# Revit family: result
name_source: partatom
category: Specialty Equipment
revit_build: Autodesk Revit 2015 (Build: 20140903_1530(x64)
units: mm (PartAtom-declared; Revit-internal decimal feet)

## types (1)
- Default
    BIMobject category = Shower trays
    BIMobject category code = sanitary-shower-trays
    BIMobject main category = Sanitary
    BIMobject main category code = sanitary
    Brand url = http://www.duravit.com
    Edition number = 1
    GTIN code = https://4053424675206
    Installation instructions = https://pro.duravit.com
    Manufacturer name = DURAVIT
    Product Guid = ccfd1b15-9e73-4d90-a85e-1945c6291bb6
    Product SKU = tempano-square-shower-tray-720188
    Product data url = https://bimobject.com
    Product family = Tempano
    Product group = shower trays
    Product name = 720188-Tempano square shower tray
    Product url = https://pro.duravit.com
    QR code = http://bimobject.com
    Technical description = https://pro.duravit.com
    Youtube clip = https://pro.duravit.com

## geometry (parser evidence)
native form markers: Sweep x2
no freeform markers — native parametric forms only
